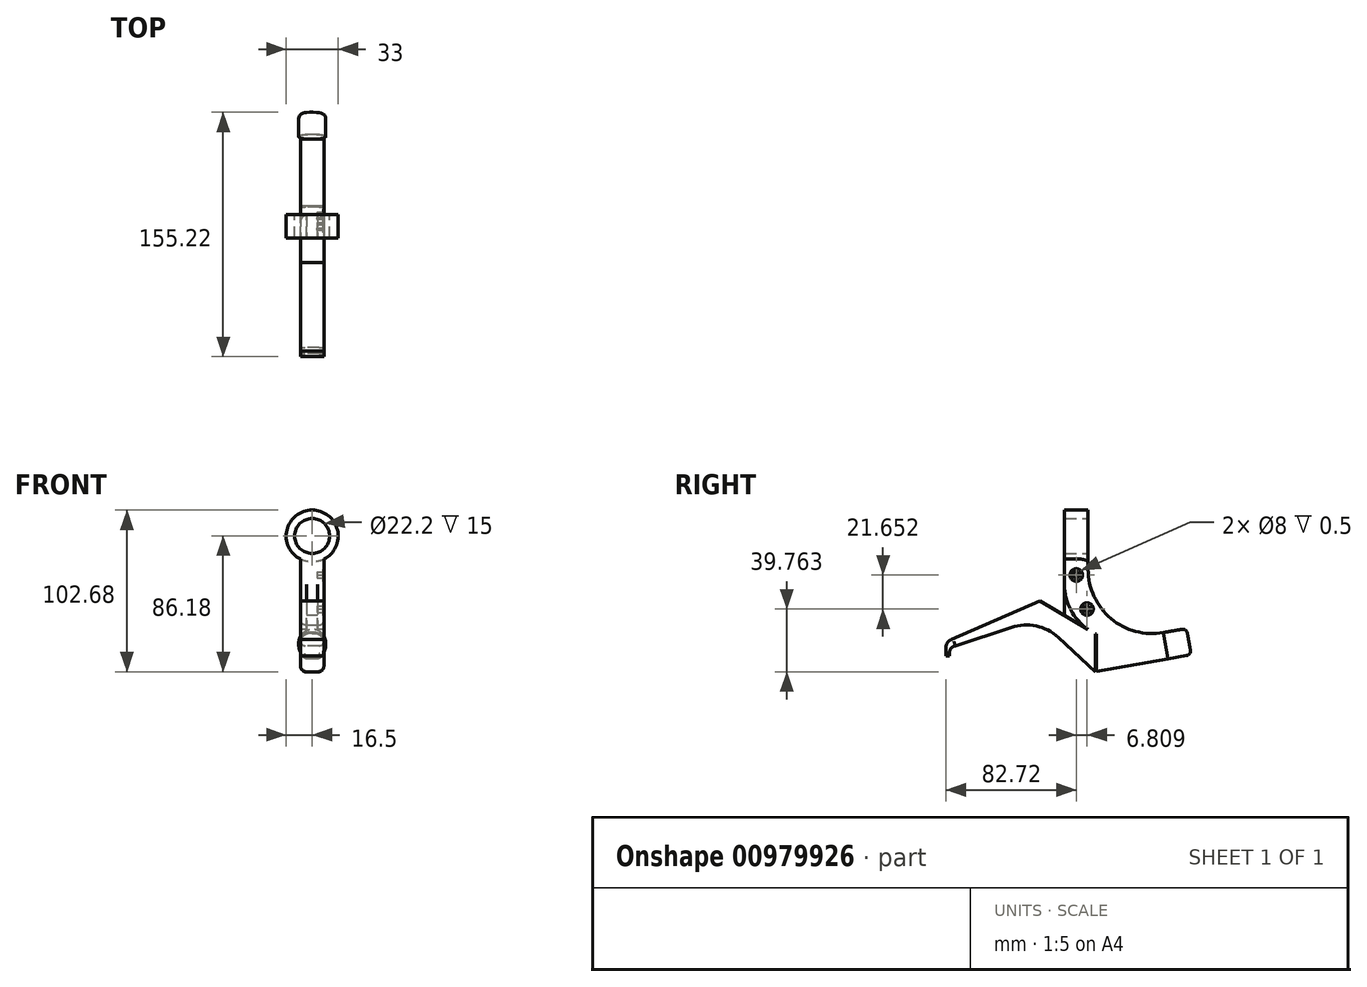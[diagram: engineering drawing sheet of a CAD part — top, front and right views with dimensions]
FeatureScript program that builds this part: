
annotation { "Feature Type Name" : "Feature", "Feature Type Description" : "" }
export const myFeature = defineFeature(function(context is Context, id is Id, definition is map)
    precondition{}
    {
        {
            var Q0;
            Q0=qCreatedBy(makeId("Front.planeOp"),FACE);
            var sketch = newSketch(context, id + "F0", { "sketchPlane" : qUnion([Q0])});
            skCircle(sketch, "E0", {"center": v(0, 0) * mm, "radius": 11.1 * mm});
            skCircle(sketch, "E1", {"center": v(0, 0) * mm, "radius": 16.5 * mm});
            skSolve(sketch);
        }
        {
            var Q0;
            Q0=makeQuery(id+"F0.imprint","IMPRINT",FACE,{"disambiguationData":[TD([[makeQuery(id+"F0.imprint","IMPRINT",EDGE,{"derivedFrom":sQuery(id+"F0.wireOp",EDGE,"E0")}),-1.0]])]});
            extrude(context, id + "F1", {"entities" : qUnion([Q0]), "depth" : 15 * mm, "symmetric" : true});
        }
        {
            var Q0;
            Q0=qCreatedBy(makeId("Right.planeOp"),FACE);
            var sketch = newSketch(context, id + "F2", { "sketchPlane" : qUnion([Q0])});
            skLineSegment(sketch, "E2", {"start": v(0, 0) * mm, "end": v(0, -54.97) * mm});
            skLineSegment(sketch, "E3", {"start": v(-7.5, 31.4) * mm, "end": v(-7.5, -50.53) * mm});
            skArc(sketch, "E4", {"start": v(-7.5, -30.7) * mm, "mid": v(-3.52, -46.9) * mm, "end": v(7.5, -59.41) * mm});
            skLineSegment(sketch, "E5", {"start": v(7.5, 51.74) * mm, "end": v(7.5, -21.27) * mm});
            skArc(sketch, "E6", {"start": v(7.5, -21.27) * mm, "mid": v(22.03, -52.44) * mm, "end": v(55.26, -61.34) * mm});
            skLineSegment(sketch, "E7", {"start": v(55.26, -61.34) * mm, "end": v(58.2, -78.08) * mm});
            skLineSegment(sketch, "E8", {"start": v(7.5, -59.41) * mm, "end": v(-23.15, -41.26) * mm});
            skLineSegment(sketch, "E9", {"start": v(-82.72, -70.49) * mm, "end": v(-82.72, -76.09) * mm});
            skLineSegment(sketch, "E10", {"start": v(-80.65, -76.09) * mm, "end": v(-80.65, -74.54) * mm});
            skLineSegment(sketch, "E11", {"start": v(-24.47, -52.49) * mm, "end": v(12.27, -86.18) * mm});
            skPoint(sketch, "E12.visualSharp", {"position": v(-80.65, -70.6) * mm});
            skArc(sketch, "E12.filletArc", {"start": v(-76.83, -69.68) * mm, "mid": v(-79.58, -71.45) * mm, "end": v(-80.65, -74.54) * mm});
            skPoint(sketch, "E13.visualSharp", {"position": v(-82.72, -66.82) * mm});
            skArc(sketch, "E13.filletArc", {"start": v(-79.22, -65.72) * mm, "mid": v(-81.75, -67.53) * mm, "end": v(-82.72, -70.49) * mm});
            skLineSegment(sketch, "E14.trimOffspring", {"start": v(12.77, -86.1) * mm, "end": v(58.2, -78.08) * mm});
            skLineSegment(sketch, "E15", {"start": v(-7.5, -13.2) * mm, "end": v(7.5, -13.2) * mm});
            skLineSegment(sketch, "E16", {"start": v(-82.72, -76.09) * mm, "end": v(-80.65, -76.09) * mm});
            skLineSegment(sketch, "E17", {"start": v(12.27, -86.18) * mm, "end": v(12.27, -62.22) * mm});
            skLineSegment(sketch, "E18", {"start": v(12.27, -62.22) * mm, "end": v(12.77, -62.22) * mm});
            skLineSegment(sketch, "E19", {"start": v(12.77, -62.22) * mm, "end": v(12.77, -86.1) * mm});
            skPoint(sketch, "E20.orphan", {"position": v(12.77, -86.18) * mm});
            skLineSegment(sketch, "E21", {"start": v(-79.22, -65.72) * mm, "end": v(-23.15, -41.26) * mm});
            skLineSegment(sketch, "E22", {"start": v(-76.83, -69.68) * mm, "end": v(-24.47, -52.49) * mm});
            skSolve(sketch);
        }
        {
            var Q0;
            {var subQ0=sQuery(id+"F2.wireOp",EDGE,"E15");var subQ1=sQuery(id+"F2.wireOp",EDGE,"E2");var subQ2=makeQuery(id+"F2.imprint","INTERSECT",VERTEX,{"derivedFrom":[subQ1,subQ0]});Q0=makeQuery(id+"F2.imprint","IMPRINT",FACE,{"disambiguationData":[TD([[makeQuery(id+"F2.imprint","IMPRINT",EDGE,{"disambiguationData":[TD([[subQ2,-1.0]])],"derivedFrom":subQ1}),-1.0]])]});}
            var Q1;
            {var subQ10=sQuery(id+"F2.wireOp",EDGE,"E6");Q1=makeQuery(id+"F2.imprint","IMPRINT",FACE,{"disambiguationData":[TD([[makeQuery(id+"F2.imprint","IMPRINT",EDGE,{"derivedFrom":subQ10}),-1.0]])]});}
            extrude(context, id + "F3", {"entities" : qUnion([Q0, Q1]), "operationType" : NewBodyOperationType.ADD, "depth" : 15 * mm, "symmetric" : true});
        }
        {
            var Q0;
            {var subQ0=sQuery(id+"F2.wireOp",EDGE,"E8");var subQ1=sQuery(id+"F2.wireOp",EDGE,"E2");var subQ2=makeQuery(id+"F2.imprint","INTERSECT",VERTEX,{"derivedFrom":[subQ1,subQ0]});Q0=makeQuery(id+"F2.imprint","IMPRINT",FACE,{"disambiguationData":[TD([[makeQuery(id+"F2.imprint","IMPRINT",EDGE,{"disambiguationData":[TD([[subQ2,1.0]])],"derivedFrom":subQ1}),-1.0]])]});}
            var Q1;
            {var subQ0=sQuery(id+"F2.wireOp",EDGE,"E8");var subQ1=sQuery(id+"F2.wireOp",EDGE,"E2");var subQ2=makeQuery(id+"F2.imprint","INTERSECT",VERTEX,{"derivedFrom":[subQ1,subQ0]});Q1=makeQuery(id+"F2.imprint","IMPRINT",FACE,{"disambiguationData":[TD([[makeQuery(id+"F2.imprint","IMPRINT",EDGE,{"disambiguationData":[TD([[subQ2,1.0]])],"derivedFrom":subQ1}),1.0]])]});}
            extrude(context, id + "F4", {"entities" : qUnion([Q0, Q1]), "operationType" : NewBodyOperationType.ADD, "depth" : 7 * mm, "symmetric" : true});
        }
        {
            var Q0;
            Q0=makeQuery(id+"F3.opExtrude","CAP_EDGE",EDGE,{"disambiguationData":[OSD([sQuery(id+"F2.wireOp",EDGE,"E6")])],"isStart":false});
            var Q1;
            Q1=makeQuery(id+"F3.opExtrude","CAP_EDGE",EDGE,{"disambiguationData":[OSD([sQuery(id+"F2.wireOp",EDGE,"E6")])],"isStart":true});
            var Q2;
            Q2=makeQuery(id+"F3.opExtrude","CAP_EDGE",EDGE,{"disambiguationData":[OSD([sQuery(id+"F2.wireOp",EDGE,"E14.trimOffspring")])],"isStart":false});
            var Q3;
            Q3=makeQuery(id+"F3.opExtrude","CAP_EDGE",EDGE,{"disambiguationData":[OSD([sQuery(id+"F2.wireOp",EDGE,"E14.trimOffspring")])],"isStart":true});
            var Q4;
            {var subQ0=sQuery(id+"F2.wireOp",EDGE,"E11");var subQ1=sQuery(id+"F2.wireOp",EDGE,"Zs4zyPn6-C5Ov-mD7S-FWXZ-QsstWJXzaYqt");Q4=makeQuery(id+"FApr9hGrNwQyOrP_1.opFillet","BLEND_EDGE",EDGE,{"blendedFrom":[makeQuery(id+"F3.opExtrude","SWEPT_EDGE",EDGE,{"disambiguationData":[OSD([subQ1,subQ0])]}),makeQuery(id+"F3.opExtrude","CAP_FACE",FACE,{"disambiguationData":[OSD([sQuery(id+"F2.wireOp",EDGE,"E3"),sQuery(id+"F2.wireOp",EDGE,"E4"),sQuery(id+"F2.wireOp",EDGE,"E5"),sQuery(id+"F2.wireOp",EDGE,"E6"),sQuery(id+"F2.wireOp",EDGE,"E7"),sQuery(id+"F2.wireOp",EDGE,"E8"),sQuery(id+"F2.wireOp",EDGE,"74US1Tta-IfNn-pP87-yXde-aIHQToQtrOJx"),sQuery(id+"F2.wireOp",EDGE,"E9"),sQuery(id+"F2.wireOp",EDGE,"E10"),subQ1,subQ0,sQuery(id+"F2.wireOp",EDGE,"E12.filletArc"),sQuery(id+"F2.wireOp",EDGE,"E13.filletArc"),sQuery(id+"F2.wireOp",EDGE,"E14.trimOffspring"),sQuery(id+"F2.wireOp",EDGE,"E15"),sQuery(id+"F2.wireOp",EDGE,"E16"),sQuery(id+"F2.wireOp",EDGE,"E17"),sQuery(id+"F2.wireOp",EDGE,"E18"),sQuery(id+"F2.wireOp",EDGE,"E19")])],"isStart":true})],"blendedInto":[makeQuery(id+"F3.opExtrude","CAP_FACE",FACE,{"disambiguationData":[OSD([sQuery(id+"F2.wireOp",EDGE,"E3"),sQuery(id+"F2.wireOp",EDGE,"E4"),sQuery(id+"F2.wireOp",EDGE,"E5"),sQuery(id+"F2.wireOp",EDGE,"E6"),sQuery(id+"F2.wireOp",EDGE,"E7"),sQuery(id+"F2.wireOp",EDGE,"E8"),sQuery(id+"F2.wireOp",EDGE,"74US1Tta-IfNn-pP87-yXde-aIHQToQtrOJx"),sQuery(id+"F2.wireOp",EDGE,"E9"),sQuery(id+"F2.wireOp",EDGE,"E10"),subQ1,subQ0,sQuery(id+"F2.wireOp",EDGE,"E12.filletArc"),sQuery(id+"F2.wireOp",EDGE,"E13.filletArc"),sQuery(id+"F2.wireOp",EDGE,"E14.trimOffspring"),sQuery(id+"F2.wireOp",EDGE,"E15"),sQuery(id+"F2.wireOp",EDGE,"E16"),sQuery(id+"F2.wireOp",EDGE,"E17"),sQuery(id+"F2.wireOp",EDGE,"E18"),sQuery(id+"F2.wireOp",EDGE,"E19")])],"isStart":true})]});}
            var Q5;
            {var subQ0=sQuery(id+"F2.wireOp",EDGE,"E11");var subQ1=sQuery(id+"F2.wireOp",EDGE,"Zs4zyPn6-C5Ov-mD7S-FWXZ-QsstWJXzaYqt");Q5=makeQuery(id+"FApr9hGrNwQyOrP_1.opFillet","BLEND_EDGE",EDGE,{"blendedFrom":[makeQuery(id+"F3.opExtrude","SWEPT_EDGE",EDGE,{"disambiguationData":[OSD([subQ1,subQ0])]}),makeQuery(id+"F3.opExtrude","CAP_FACE",FACE,{"disambiguationData":[OSD([sQuery(id+"F2.wireOp",EDGE,"E3"),sQuery(id+"F2.wireOp",EDGE,"E4"),sQuery(id+"F2.wireOp",EDGE,"E5"),sQuery(id+"F2.wireOp",EDGE,"E6"),sQuery(id+"F2.wireOp",EDGE,"E7"),sQuery(id+"F2.wireOp",EDGE,"E8"),sQuery(id+"F2.wireOp",EDGE,"74US1Tta-IfNn-pP87-yXde-aIHQToQtrOJx"),sQuery(id+"F2.wireOp",EDGE,"E9"),sQuery(id+"F2.wireOp",EDGE,"E10"),subQ1,subQ0,sQuery(id+"F2.wireOp",EDGE,"E12.filletArc"),sQuery(id+"F2.wireOp",EDGE,"E13.filletArc"),sQuery(id+"F2.wireOp",EDGE,"E14.trimOffspring"),sQuery(id+"F2.wireOp",EDGE,"E15"),sQuery(id+"F2.wireOp",EDGE,"E16"),sQuery(id+"F2.wireOp",EDGE,"E17"),sQuery(id+"F2.wireOp",EDGE,"E18"),sQuery(id+"F2.wireOp",EDGE,"E19")])],"isStart":false})],"blendedInto":[makeQuery(id+"F3.opExtrude","CAP_FACE",FACE,{"disambiguationData":[OSD([sQuery(id+"F2.wireOp",EDGE,"E3"),sQuery(id+"F2.wireOp",EDGE,"E4"),sQuery(id+"F2.wireOp",EDGE,"E5"),sQuery(id+"F2.wireOp",EDGE,"E6"),sQuery(id+"F2.wireOp",EDGE,"E7"),sQuery(id+"F2.wireOp",EDGE,"E8"),sQuery(id+"F2.wireOp",EDGE,"74US1Tta-IfNn-pP87-yXde-aIHQToQtrOJx"),sQuery(id+"F2.wireOp",EDGE,"E9"),sQuery(id+"F2.wireOp",EDGE,"E10"),subQ1,subQ0,sQuery(id+"F2.wireOp",EDGE,"E12.filletArc"),sQuery(id+"F2.wireOp",EDGE,"E13.filletArc"),sQuery(id+"F2.wireOp",EDGE,"E14.trimOffspring"),sQuery(id+"F2.wireOp",EDGE,"E15"),sQuery(id+"F2.wireOp",EDGE,"E16"),sQuery(id+"F2.wireOp",EDGE,"E17"),sQuery(id+"F2.wireOp",EDGE,"E18"),sQuery(id+"F2.wireOp",EDGE,"E19")])],"isStart":false})]});}
            fillet(context, id + "F5", {"entities" : qUnion([Q0, Q1, Q2, Q3, Q4, Q5]), "radius" : 5 * mm, "tangentPropagation" : true, "allowEdgeOverflow" : false});
        }
        {
            var Q0;
            Q0=makeQuery(id+"F3.opExtrude","SWEPT_FACE",FACE,{"disambiguationData":[OSD([sQuery(id+"F2.wireOp",EDGE,"E7")])]});
            var sketch = newSketch(context, id + "F6", { "sketchPlane" : qUnion([Q0])});
            skCircle(sketch, "E23", {"center": v(0, -78.5) * mm, "radius": 8.5 * mm});
            skPoint(sketch, "E23.centerSnap0", {"position": v(-7.5, -78.5) * mm});
            skSolve(sketch);
        }
        {
            var Q0;
            {var subQ2=sQuery(id+"F2.wireOp",EDGE,"E7");var subQ16=makeQuery(id+"F3.opExtrude","CAP_EDGE",EDGE,{"disambiguationData":[OSD([subQ2])],"isStart":true});Q0=makeQuery(id+"F6.imprint","IMPRINT",FACE,{"disambiguationData":[TD([[makeQuery(id+"F6.imprint","IMPRINT",EDGE,{"derivedFrom":subQ16}),-1.0]])]});}
            var Q1;
            {var subQ1=sQuery(id+"F2.wireOp",EDGE,"E7");var subQ7=makeQuery(id+"F3.opExtrude","CAP_EDGE",EDGE,{"disambiguationData":[OSD([subQ1])],"isStart":false});Q1=makeQuery(id+"F6.imprint","IMPRINT",FACE,{"disambiguationData":[TD([[makeQuery(id+"F6.imprint","IMPRINT",EDGE,{"derivedFrom":subQ7}),-1.0]])]});}
            var Q2;
            {var subQ1=sQuery(id+"F2.wireOp",EDGE,"E7");var subQ7=makeQuery(id+"F3.opExtrude","CAP_EDGE",EDGE,{"disambiguationData":[OSD([subQ1])],"isStart":true});Q2=makeQuery(id+"F6.imprint","IMPRINT",FACE,{"disambiguationData":[TD([[makeQuery(id+"F6.imprint","IMPRINT",EDGE,{"derivedFrom":subQ7}),1.0]])]});}
            extrude(context, id + "F7", {"entities" : qUnion([Q0, Q1, Q2]), "operationType" : NewBodyOperationType.ADD, "depth" : 15 * mm});
        }
        {
            var Q0;
            Q0=makeQuery(id+"F7.opExtrude","CAP_EDGE",EDGE,{"disambiguationData":[OSD([sQuery(id+"F6.wireOp",EDGE,"E23")])],"isStart":false});
            fillet(context, id + "F8", {"entities" : qUnion([Q0]), "radius" : 3 * mm, "tangentPropagation" : true, "allowEdgeOverflow" : false});
        }
        {
            var Q0;
            Q0=makeQuery(id+"F3.opExtrude","SWEPT_EDGE",EDGE,{"disambiguationData":[OSD([sQuery(id+"F2.wireOp",EDGE,"E11"),sQuery(id+"F2.wireOp",EDGE,"E22")])]});
            fillet(context, id + "F9", {"entities" : qUnion([Q0]), "radius" : 30 * mm, "tangentPropagation" : true, "allowEdgeOverflow" : false});
        }
        {
            var Q0;
            Q0=makeQuery(id+"F3.opExtrude","CAP_EDGE",EDGE,{"disambiguationData":[OSD([sQuery(id+"F2.wireOp",EDGE,"E11")])],"isStart":false});
            var Q1;
            Q1=makeQuery(id+"F3.opExtrude","CAP_EDGE",EDGE,{"disambiguationData":[OSD([sQuery(id+"F2.wireOp",EDGE,"E11")])],"isStart":true});
            fillet(context, id + "F10", {"entities" : qUnion([Q0, Q1]), "radius" : 3 * mm, "tangentPropagation" : true, "allowEdgeOverflow" : false});
        }
        {
            var Q0;
            Q0=makeQuery(id+"F3.opExtrude","CAP_FACE",FACE,{"disambiguationData":[OSD([sQuery(id+"F2.wireOp",EDGE,"E3"),sQuery(id+"F2.wireOp",EDGE,"E4"),sQuery(id+"F2.wireOp",EDGE,"E5"),sQuery(id+"F2.wireOp",EDGE,"E6"),sQuery(id+"F2.wireOp",EDGE,"E7"),sQuery(id+"F2.wireOp",EDGE,"E8"),sQuery(id+"F2.wireOp",EDGE,"E9"),sQuery(id+"F2.wireOp",EDGE,"E10"),sQuery(id+"F2.wireOp",EDGE,"E11"),sQuery(id+"F2.wireOp",EDGE,"E12.filletArc"),sQuery(id+"F2.wireOp",EDGE,"E13.filletArc"),sQuery(id+"F2.wireOp",EDGE,"E14.trimOffspring"),sQuery(id+"F2.wireOp",EDGE,"E15"),sQuery(id+"F2.wireOp",EDGE,"E16"),sQuery(id+"F2.wireOp",EDGE,"E17"),sQuery(id+"F2.wireOp",EDGE,"E18"),sQuery(id+"F2.wireOp",EDGE,"E19"),sQuery(id+"F2.wireOp",EDGE,"E21"),sQuery(id+"F2.wireOp",EDGE,"E22")])],"isStart":false});
            var sketch = newSketch(context, id + "F11", { "sketchPlane" : qUnion([Q0])});
            skCircle(sketch, "E24", {"center": v(0, -24.77) * mm, "radius": 4 * mm});
            skCircle(sketch, "E25", {"center": v(6.8, -46.42) * mm, "radius": 4 * mm});
            skSolve(sketch);
        }
        {
            var Q0;
            {var subQ0=sQuery(id+"F11.wireOp",EDGE,"E24");var subQ1=sQuery(id+"F2.wireOp",EDGE,"E6");var subQ2=makeQuery(id+"F5.opFillet","BLEND_EDGE",EDGE,{"blendedFrom":[makeQuery(id+"F3.opExtrude","CAP_EDGE",EDGE,{"disambiguationData":[OSD([subQ1])],"isStart":false}),makeQuery(id+"F3.opExtrude","CAP_FACE",FACE,{"disambiguationData":[OSD([sQuery(id+"F2.wireOp",EDGE,"E3"),sQuery(id+"F2.wireOp",EDGE,"E4"),sQuery(id+"F2.wireOp",EDGE,"E5"),subQ1,sQuery(id+"F2.wireOp",EDGE,"E7"),sQuery(id+"F2.wireOp",EDGE,"E8"),sQuery(id+"F2.wireOp",EDGE,"E9"),sQuery(id+"F2.wireOp",EDGE,"E10"),sQuery(id+"F2.wireOp",EDGE,"E11"),sQuery(id+"F2.wireOp",EDGE,"E12.filletArc"),sQuery(id+"F2.wireOp",EDGE,"E13.filletArc"),sQuery(id+"F2.wireOp",EDGE,"E14.trimOffspring"),sQuery(id+"F2.wireOp",EDGE,"E15"),sQuery(id+"F2.wireOp",EDGE,"E16"),sQuery(id+"F2.wireOp",EDGE,"E17"),sQuery(id+"F2.wireOp",EDGE,"E18"),sQuery(id+"F2.wireOp",EDGE,"E19"),sQuery(id+"F2.wireOp",EDGE,"E21"),sQuery(id+"F2.wireOp",EDGE,"E22")])],"isStart":false})],"blendedInto":[makeQuery(id+"F3.opExtrude","CAP_FACE",FACE,{"disambiguationData":[OSD([sQuery(id+"F2.wireOp",EDGE,"E3"),sQuery(id+"F2.wireOp",EDGE,"E4"),sQuery(id+"F2.wireOp",EDGE,"E5"),subQ1,sQuery(id+"F2.wireOp",EDGE,"E7"),sQuery(id+"F2.wireOp",EDGE,"E8"),sQuery(id+"F2.wireOp",EDGE,"E9"),sQuery(id+"F2.wireOp",EDGE,"E10"),sQuery(id+"F2.wireOp",EDGE,"E11"),sQuery(id+"F2.wireOp",EDGE,"E12.filletArc"),sQuery(id+"F2.wireOp",EDGE,"E13.filletArc"),sQuery(id+"F2.wireOp",EDGE,"E14.trimOffspring"),sQuery(id+"F2.wireOp",EDGE,"E15"),sQuery(id+"F2.wireOp",EDGE,"E16"),sQuery(id+"F2.wireOp",EDGE,"E17"),sQuery(id+"F2.wireOp",EDGE,"E18"),sQuery(id+"F2.wireOp",EDGE,"E19"),sQuery(id+"F2.wireOp",EDGE,"E21"),sQuery(id+"F2.wireOp",EDGE,"E22")])],"isStart":false})]});var subQ3=makeQuery(id+"F11.imprint","INTERSECT",VERTEX,{"disambiguationData":[OD(0.0)],"derivedFrom":[subQ2,subQ0]});Q0=makeQuery(id+"F11.imprint","IMPRINT",FACE,{"disambiguationData":[TD([[makeQuery(id+"F11.imprint","IMPRINT",EDGE,{"disambiguationData":[TD([[subQ3,1.0]])],"derivedFrom":subQ0}),1.0]])]});}
            var Q1;
            {var subQ0=sQuery(id+"F11.wireOp",EDGE,"E25");var subQ1=sQuery(id+"F2.wireOp",EDGE,"E6");var subQ2=makeQuery(id+"F5.opFillet","BLEND_EDGE",EDGE,{"blendedFrom":[makeQuery(id+"F3.opExtrude","CAP_EDGE",EDGE,{"disambiguationData":[OSD([subQ1])],"isStart":false}),makeQuery(id+"F3.opExtrude","CAP_FACE",FACE,{"disambiguationData":[OSD([sQuery(id+"F2.wireOp",EDGE,"E3"),sQuery(id+"F2.wireOp",EDGE,"E4"),sQuery(id+"F2.wireOp",EDGE,"E5"),subQ1,sQuery(id+"F2.wireOp",EDGE,"E7"),sQuery(id+"F2.wireOp",EDGE,"E8"),sQuery(id+"F2.wireOp",EDGE,"E9"),sQuery(id+"F2.wireOp",EDGE,"E10"),sQuery(id+"F2.wireOp",EDGE,"E11"),sQuery(id+"F2.wireOp",EDGE,"E12.filletArc"),sQuery(id+"F2.wireOp",EDGE,"E13.filletArc"),sQuery(id+"F2.wireOp",EDGE,"E14.trimOffspring"),sQuery(id+"F2.wireOp",EDGE,"E15"),sQuery(id+"F2.wireOp",EDGE,"E16"),sQuery(id+"F2.wireOp",EDGE,"E17"),sQuery(id+"F2.wireOp",EDGE,"E18"),sQuery(id+"F2.wireOp",EDGE,"E19"),sQuery(id+"F2.wireOp",EDGE,"E21"),sQuery(id+"F2.wireOp",EDGE,"E22")])],"isStart":false})],"blendedInto":[makeQuery(id+"F3.opExtrude","CAP_FACE",FACE,{"disambiguationData":[OSD([sQuery(id+"F2.wireOp",EDGE,"E3"),sQuery(id+"F2.wireOp",EDGE,"E4"),sQuery(id+"F2.wireOp",EDGE,"E5"),subQ1,sQuery(id+"F2.wireOp",EDGE,"E7"),sQuery(id+"F2.wireOp",EDGE,"E8"),sQuery(id+"F2.wireOp",EDGE,"E9"),sQuery(id+"F2.wireOp",EDGE,"E10"),sQuery(id+"F2.wireOp",EDGE,"E11"),sQuery(id+"F2.wireOp",EDGE,"E12.filletArc"),sQuery(id+"F2.wireOp",EDGE,"E13.filletArc"),sQuery(id+"F2.wireOp",EDGE,"E14.trimOffspring"),sQuery(id+"F2.wireOp",EDGE,"E15"),sQuery(id+"F2.wireOp",EDGE,"E16"),sQuery(id+"F2.wireOp",EDGE,"E17"),sQuery(id+"F2.wireOp",EDGE,"E18"),sQuery(id+"F2.wireOp",EDGE,"E19"),sQuery(id+"F2.wireOp",EDGE,"E21"),sQuery(id+"F2.wireOp",EDGE,"E22")])],"isStart":false})]});var subQ3=makeQuery(id+"F11.imprint","INTERSECT",VERTEX,{"disambiguationData":[OD(0.0)],"derivedFrom":[subQ2,subQ0]});Q1=makeQuery(id+"F11.imprint","IMPRINT",FACE,{"disambiguationData":[TD([[makeQuery(id+"F11.imprint","IMPRINT",EDGE,{"disambiguationData":[TD([[subQ3,-1.0]])],"derivedFrom":subQ0}),1.0]])]});}
            var Q2;
            {var subQ0=sQuery(id+"F11.wireOp",EDGE,"E25");var subQ1=sQuery(id+"F2.wireOp",EDGE,"E6");var subQ2=makeQuery(id+"F5.opFillet","BLEND_EDGE",EDGE,{"blendedFrom":[makeQuery(id+"F3.opExtrude","CAP_EDGE",EDGE,{"disambiguationData":[OSD([subQ1])],"isStart":false}),makeQuery(id+"F3.opExtrude","CAP_FACE",FACE,{"disambiguationData":[OSD([sQuery(id+"F2.wireOp",EDGE,"E3"),sQuery(id+"F2.wireOp",EDGE,"E4"),sQuery(id+"F2.wireOp",EDGE,"E5"),subQ1,sQuery(id+"F2.wireOp",EDGE,"E7"),sQuery(id+"F2.wireOp",EDGE,"E8"),sQuery(id+"F2.wireOp",EDGE,"E9"),sQuery(id+"F2.wireOp",EDGE,"E10"),sQuery(id+"F2.wireOp",EDGE,"E11"),sQuery(id+"F2.wireOp",EDGE,"E12.filletArc"),sQuery(id+"F2.wireOp",EDGE,"E13.filletArc"),sQuery(id+"F2.wireOp",EDGE,"E14.trimOffspring"),sQuery(id+"F2.wireOp",EDGE,"E15"),sQuery(id+"F2.wireOp",EDGE,"E16"),sQuery(id+"F2.wireOp",EDGE,"E17"),sQuery(id+"F2.wireOp",EDGE,"E18"),sQuery(id+"F2.wireOp",EDGE,"E19"),sQuery(id+"F2.wireOp",EDGE,"E21"),sQuery(id+"F2.wireOp",EDGE,"E22")])],"isStart":false})],"blendedInto":[makeQuery(id+"F3.opExtrude","CAP_FACE",FACE,{"disambiguationData":[OSD([sQuery(id+"F2.wireOp",EDGE,"E3"),sQuery(id+"F2.wireOp",EDGE,"E4"),sQuery(id+"F2.wireOp",EDGE,"E5"),subQ1,sQuery(id+"F2.wireOp",EDGE,"E7"),sQuery(id+"F2.wireOp",EDGE,"E8"),sQuery(id+"F2.wireOp",EDGE,"E9"),sQuery(id+"F2.wireOp",EDGE,"E10"),sQuery(id+"F2.wireOp",EDGE,"E11"),sQuery(id+"F2.wireOp",EDGE,"E12.filletArc"),sQuery(id+"F2.wireOp",EDGE,"E13.filletArc"),sQuery(id+"F2.wireOp",EDGE,"E14.trimOffspring"),sQuery(id+"F2.wireOp",EDGE,"E15"),sQuery(id+"F2.wireOp",EDGE,"E16"),sQuery(id+"F2.wireOp",EDGE,"E17"),sQuery(id+"F2.wireOp",EDGE,"E18"),sQuery(id+"F2.wireOp",EDGE,"E19"),sQuery(id+"F2.wireOp",EDGE,"E21"),sQuery(id+"F2.wireOp",EDGE,"E22")])],"isStart":false})]});var subQ3=makeQuery(id+"F11.imprint","INTERSECT",VERTEX,{"disambiguationData":[OD(0.0)],"derivedFrom":[subQ2,subQ0]});Q2=makeQuery(id+"F11.imprint","IMPRINT",FACE,{"disambiguationData":[TD([[makeQuery(id+"F11.imprint","IMPRINT",EDGE,{"disambiguationData":[TD([[subQ3,1.0]])],"derivedFrom":subQ0}),1.0]])]});}
            var Q3;
            {var subQ0=sQuery(id+"F11.wireOp",EDGE,"E24");var subQ1=sQuery(id+"F2.wireOp",EDGE,"E6");var subQ2=makeQuery(id+"F5.opFillet","BLEND_EDGE",EDGE,{"blendedFrom":[makeQuery(id+"F3.opExtrude","CAP_EDGE",EDGE,{"disambiguationData":[OSD([subQ1])],"isStart":false}),makeQuery(id+"F3.opExtrude","CAP_FACE",FACE,{"disambiguationData":[OSD([sQuery(id+"F2.wireOp",EDGE,"E3"),sQuery(id+"F2.wireOp",EDGE,"E4"),sQuery(id+"F2.wireOp",EDGE,"E5"),subQ1,sQuery(id+"F2.wireOp",EDGE,"E7"),sQuery(id+"F2.wireOp",EDGE,"E8"),sQuery(id+"F2.wireOp",EDGE,"E9"),sQuery(id+"F2.wireOp",EDGE,"E10"),sQuery(id+"F2.wireOp",EDGE,"E11"),sQuery(id+"F2.wireOp",EDGE,"E12.filletArc"),sQuery(id+"F2.wireOp",EDGE,"E13.filletArc"),sQuery(id+"F2.wireOp",EDGE,"E14.trimOffspring"),sQuery(id+"F2.wireOp",EDGE,"E15"),sQuery(id+"F2.wireOp",EDGE,"E16"),sQuery(id+"F2.wireOp",EDGE,"E17"),sQuery(id+"F2.wireOp",EDGE,"E18"),sQuery(id+"F2.wireOp",EDGE,"E19"),sQuery(id+"F2.wireOp",EDGE,"E21"),sQuery(id+"F2.wireOp",EDGE,"E22")])],"isStart":false})],"blendedInto":[makeQuery(id+"F3.opExtrude","CAP_FACE",FACE,{"disambiguationData":[OSD([sQuery(id+"F2.wireOp",EDGE,"E3"),sQuery(id+"F2.wireOp",EDGE,"E4"),sQuery(id+"F2.wireOp",EDGE,"E5"),subQ1,sQuery(id+"F2.wireOp",EDGE,"E7"),sQuery(id+"F2.wireOp",EDGE,"E8"),sQuery(id+"F2.wireOp",EDGE,"E9"),sQuery(id+"F2.wireOp",EDGE,"E10"),sQuery(id+"F2.wireOp",EDGE,"E11"),sQuery(id+"F2.wireOp",EDGE,"E12.filletArc"),sQuery(id+"F2.wireOp",EDGE,"E13.filletArc"),sQuery(id+"F2.wireOp",EDGE,"E14.trimOffspring"),sQuery(id+"F2.wireOp",EDGE,"E15"),sQuery(id+"F2.wireOp",EDGE,"E16"),sQuery(id+"F2.wireOp",EDGE,"E17"),sQuery(id+"F2.wireOp",EDGE,"E18"),sQuery(id+"F2.wireOp",EDGE,"E19"),sQuery(id+"F2.wireOp",EDGE,"E21"),sQuery(id+"F2.wireOp",EDGE,"E22")])],"isStart":false})]});var subQ3=makeQuery(id+"F11.imprint","INTERSECT",VERTEX,{"disambiguationData":[OD(0.0)],"derivedFrom":[subQ2,subQ0]});Q3=makeQuery(id+"F11.imprint","IMPRINT",FACE,{"disambiguationData":[TD([[makeQuery(id+"F11.imprint","IMPRINT",EDGE,{"disambiguationData":[TD([[subQ3,-1.0]])],"derivedFrom":subQ0}),1.0]])]});}
            extrude(context, id + "F12", {"entities" : qUnion([Q0, Q1, Q2, Q3]), "operationType" : NewBodyOperationType.REMOVE, "oppositeDirection" : true, "depth" : 0.5 * mm});
        }
        {
            var Q0;
            Q0=makeQuery(id+"F12.boolean.opBoolean","COPY",FACE,{"derivedFrom":makeQuery(id+"F12.opExtrude","CAP_FACE",FACE,{"disambiguationData":[OSD([sQuery(id+"F11.wireOp",EDGE,"E24")])],"isStart":false})});
            var sketch = newSketch(context, id + "F13", { "sketchPlane" : qUnion([Q0])});
            skCircle(sketch, "E26.cCircle", {"center": v(0, -24.77) * mm, "radius": 2 * mm, "construction": true});
            skLineSegment(sketch, "E26.0", {"start": v(1.15, -26.77) * mm, "end": v(-1.15, -26.77) * mm});
            skLineSegment(sketch, "E26.1", {"start": v(-1.15, -26.77) * mm, "end": v(-2.3, -24.77) * mm});
            skLineSegment(sketch, "E26.2", {"start": v(-2.3, -24.77) * mm, "end": v(-1.15, -22.77) * mm});
            skLineSegment(sketch, "E26.3", {"start": v(-1.15, -22.77) * mm, "end": v(1.15, -22.77) * mm});
            skLineSegment(sketch, "E26.4", {"start": v(1.15, -22.77) * mm, "end": v(2.3, -24.77) * mm});
            skLineSegment(sketch, "E26.5", {"start": v(2.3, -24.77) * mm, "end": v(1.15, -26.77) * mm});
            skPoint(sketch, "E26.0.midPoint", {"position": v(0, -26.77) * mm});
            skSolve(sketch);
        }
        {
            var Q0;
            Q0=makeQuery(id+"F13.imprint","IMPRINT",FACE,{"disambiguationData":[TD([[makeQuery(id+"F13.imprint","IMPRINT",EDGE,{"derivedFrom":sQuery(id+"F13.wireOp",EDGE,"E26.0")}),-1.0]])]});
            extrude(context, id + "F14", {"entities" : qUnion([Q0]), "operationType" : NewBodyOperationType.REMOVE, "oppositeDirection" : true, "depth" : 4 * mm});
        }
        {
            var Q0;
            Q0=makeQuery(id+"F12.boolean.opBoolean","COPY",FACE,{"derivedFrom":makeQuery(id+"F12.opExtrude","CAP_FACE",FACE,{"disambiguationData":[OSD([sQuery(id+"F11.wireOp",EDGE,"E25")])],"isStart":false})});
            var sketch = newSketch(context, id + "F15", { "sketchPlane" : qUnion([Q0])});
            skCircle(sketch, "E27.cCircle", {"center": v(6.8, -46.42) * mm, "radius": 2 * mm, "construction": true});
            skLineSegment(sketch, "E27.0", {"start": v(7.96, -48.42) * mm, "end": v(5.65, -48.42) * mm});
            skLineSegment(sketch, "E27.1", {"start": v(5.65, -48.42) * mm, "end": v(4.5, -46.42) * mm});
            skLineSegment(sketch, "E27.2", {"start": v(4.5, -46.42) * mm, "end": v(5.65, -44.42) * mm});
            skLineSegment(sketch, "E27.3", {"start": v(5.65, -44.42) * mm, "end": v(7.96, -44.42) * mm});
            skLineSegment(sketch, "E27.4", {"start": v(7.96, -44.42) * mm, "end": v(9.12, -46.42) * mm});
            skLineSegment(sketch, "E27.5", {"start": v(9.12, -46.42) * mm, "end": v(7.96, -48.42) * mm});
            skPoint(sketch, "E27.0.midPoint", {"position": v(6.8, -48.42) * mm});
            skSolve(sketch);
        }
        {
            var Q0;
            Q0=makeQuery(id+"F15.imprint","IMPRINT",FACE,{"disambiguationData":[TD([[makeQuery(id+"F15.imprint","IMPRINT",EDGE,{"derivedFrom":sQuery(id+"F15.wireOp",EDGE,"E27.0")}),-1.0]])]});
            extrude(context, id + "F16", {"entities" : qUnion([Q0]), "operationType" : NewBodyOperationType.REMOVE, "oppositeDirection" : true, "depth" : 4 * mm});
        }
    });
